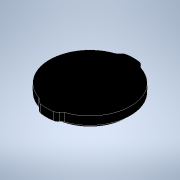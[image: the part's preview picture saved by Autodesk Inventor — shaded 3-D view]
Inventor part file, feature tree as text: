
AUTODESK INVENTOR PART (.ipt)
format: ipt  version: 2022 (Build 260153000, 153)  size: 168,960 bytes
history: native  units: in
note: dims shown in document units (in); Inventor stores cm internally (conversion verified against a paired STEP export)
features: sketch x4, extrude x3, fillet x2, pattern_circular x1, revolve x1
ambient origin geometry x8: Origin, YZ Plane, XZ Plane, XY Plane, X Axis, Y Axis, Z Axis, Center Point
bodies: Solid1 (feature_tree)
feature tree (11):
  extrude  "Extrusion1"  Depth=0.1181in TaperAngle=0.0deg
  extrude  "Extrusion2"  Depth=0.2283in TaperAngle=0.0deg
  extrude  "Extrusion4"  Depth=0.3937in
  fillet  "Fillet2"  Radius=0.6299in
  pattern_circular  "Circular Pattern1"  [2 undecoded]
  revolve  "Revolution1"  [1 undecoded]
  fillet  "Fillet3"  [1 undecoded]
  sketch  "Sketch1"  dims[d0=2.0256in d1=0.1181in d2=0.0in]
  sketch  "Sketch2"  dims[d3=2.2677in d4=0.2283in d5=0.0in]
  sketch  "Sketch5"  dims[d28=0.3937in d29=0.0in d30=0.1575in d33=0.6299in]
  sketch  "Sketch6"  dims[d34=1.0892in d35=1.0892in d36=0.1181in d37=120.0deg d38=0.1181in d39=60.0deg d40=1.1339in d41=0.7874in d42=360.0deg d44=0.1211in d45=0.0787in d46=0.0394in d47=0.086in d48=0.086in d49=0.0197in]
note: 4 required parameter values undecoded (feature->parameter linkage not recoverable at this tier; creation-order binding heuristic only, values carry confidence <= 0.55)